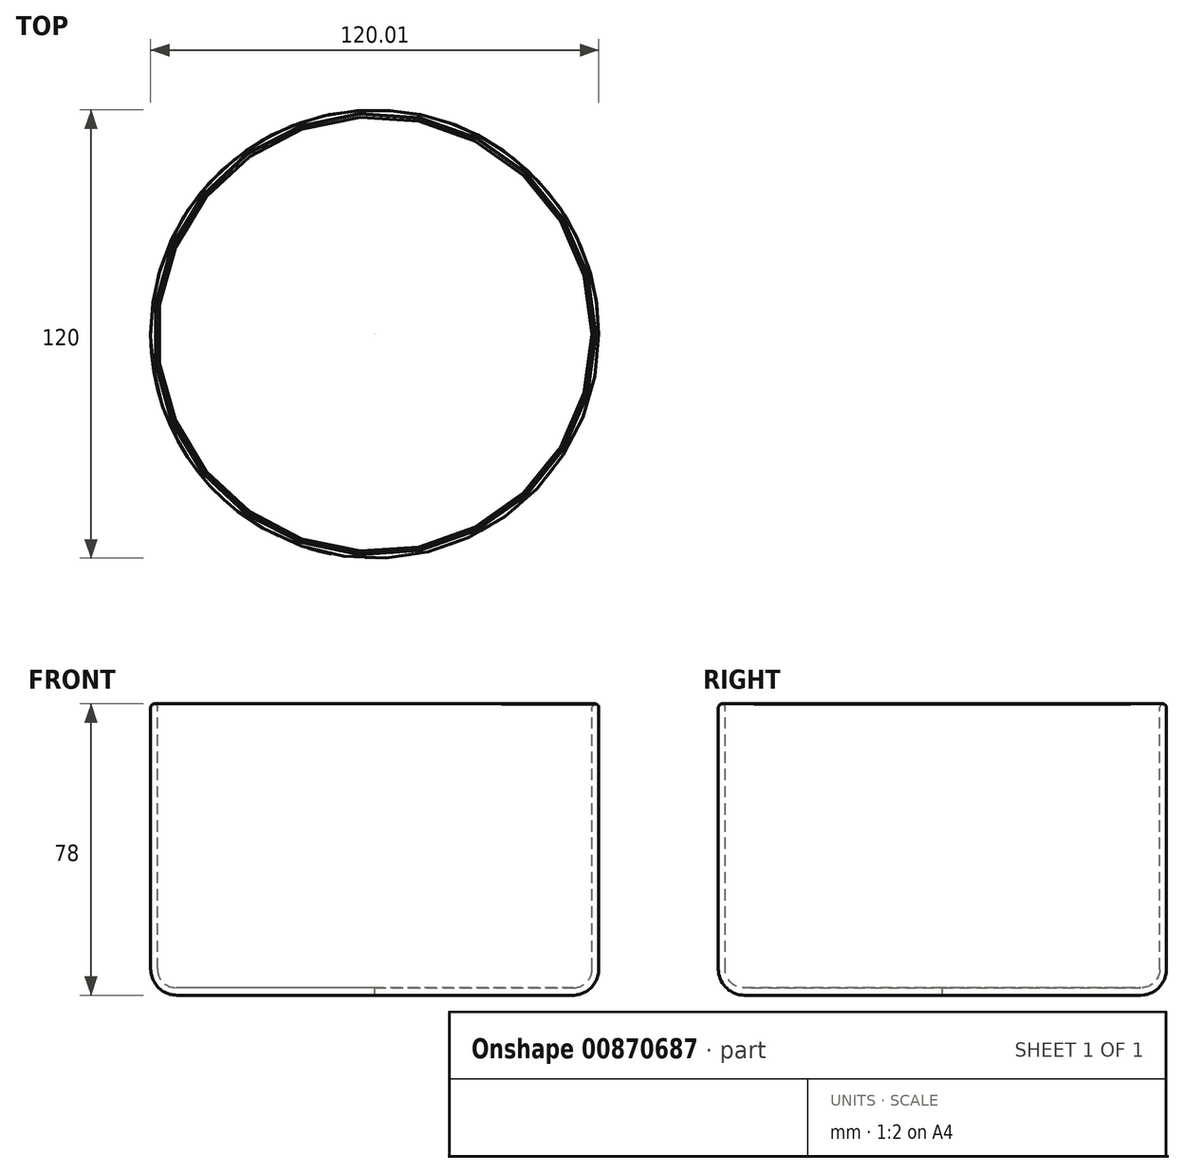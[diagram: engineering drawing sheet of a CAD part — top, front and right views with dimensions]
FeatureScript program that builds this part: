
annotation { "Feature Type Name" : "Feature", "Feature Type Description" : "" }
export const myFeature = defineFeature(function(context is Context, id is Id, definition is map)
    precondition{}
    {
        {
            var Q0;
            Q0=qCreatedBy(makeId("Front.planeOp"),FACE);
            var sketch = newSketch(context, id + "F0", { "sketchPlane" : qUnion([Q0])});
            skLineSegment(sketch, "E0", {"start": v(0, -68) * mm, "end": v(-53.2, -68) * mm});
            skLineSegment(sketch, "E1", {"start": v(-58.2, -63) * mm, "end": v(-58.2, 7) * mm});
            skLineSegment(sketch, "E2", {"start": v(-59, 8) * mm, "end": v(-59.2, 8) * mm});
            skLineSegment(sketch, "E3", {"start": v(-60, 7) * mm, "end": v(-60, -63) * mm});
            skLineSegment(sketch, "E4", {"start": v(-53, -70) * mm, "end": v(0, -70) * mm});
            skLineSegment(sketch, "E5", {"start": v(0, -70) * mm, "end": v(0, -68) * mm});
            skLineSegment(sketch, "E6", {"start": v(0, 0.19) * mm, "end": v(0, -90.13) * mm, "construction": true});
            skPoint(sketch, "E7.visualSharp", {"position": v(-58.2, -68) * mm});
            skArc(sketch, "E7.filletArc", {"start": v(-58.2, -63) * mm, "mid": v(-56.74, -66.54) * mm, "end": v(-53.2, -68) * mm});
            skPoint(sketch, "E8.visualSharp", {"position": v(-60, -70) * mm});
            skArc(sketch, "E8.filletArc", {"start": v(-60, -63) * mm, "mid": v(-57.95, -67.95) * mm, "end": v(-53, -70) * mm});
            skPoint(sketch, "E9.visualSharp", {"position": v(-60, 8) * mm});
            skArc(sketch, "E9.filletArc", {"start": v(-59, 8) * mm, "mid": v(-59.7, 7.7) * mm, "end": v(-60, 7) * mm});
            skPoint(sketch, "E10.visualSharp", {"position": v(-58.2, 8) * mm});
            skArc(sketch, "E10.filletArc", {"start": v(-58.2, 7) * mm, "mid": v(-58.5, 7.7) * mm, "end": v(-59.2, 8) * mm});
            skSolve(sketch);
        }
        {
            var Q0;
            Q0 = qSketchRegion(id + "F0", true);
            var Q1;
            Q1=sQuery(id+"F0.wireOp",EDGE,"E6");
            revolve(context, id + "F1", {"surfaceOperationType" : NewSurfaceOperationType.NEW, "entities" : qUnion([Q0]), "axis" : qUnion([Q1]), "revolveType" : RevolveType.FULL});
        }
    });
